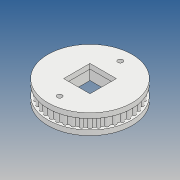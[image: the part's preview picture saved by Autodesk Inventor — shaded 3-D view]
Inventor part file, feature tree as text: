
AUTODESK INVENTOR PART (.ipt)
format: ipt  version: 2017 (Build 210142000, 142)  size: 267,264 bytes
history: native  units: mm
features: other x5, reference x5, extrude x3, sketch x3
ambient origin geometry x8: Origin, YZ Plane, XZ Plane, XY Plane, X Axis, Y Axis, Z Axis, Center Point
bodies: Body1 (feature_tree), Body2 (feature_tree), Body3 (feature_tree)
feature tree (16):
  other  "Sólido1"
  extrude  "Extrusión1"  Depth=6.0mm TaperAngle=0.0deg
  extrude  "Extrusión2"  Depth=3.0mm
  extrude  "Extrusión3"  Depth=3.0mm
  sketch  "Boceto1"  dims[d0=46.9mm d1=6.0mm d2=0.0mm]
  reference  "Referencia1"
  sketch  "Boceto2"  dims[d3=3.0mm d4=5.0mm]
  other  "Sólido2"
  sketch  "Boceto3"  dims[d5=20.0mm d7=360.0deg d9=31.0mm d11=3.0mm d12=0.0mm d16=2.0mm d17=400.0mm d19=360.0deg d21=51.0mm d22=3.0mm d23=0.0mm d24=48.9mm]
  reference  "Referencia2"
  reference  "Referencia3"
  reference  "Referencia4"
  reference  "Referencia5"
  other  "Sólido3"
  other  "Polea motor.iam"
  other  "dado polea:1"
